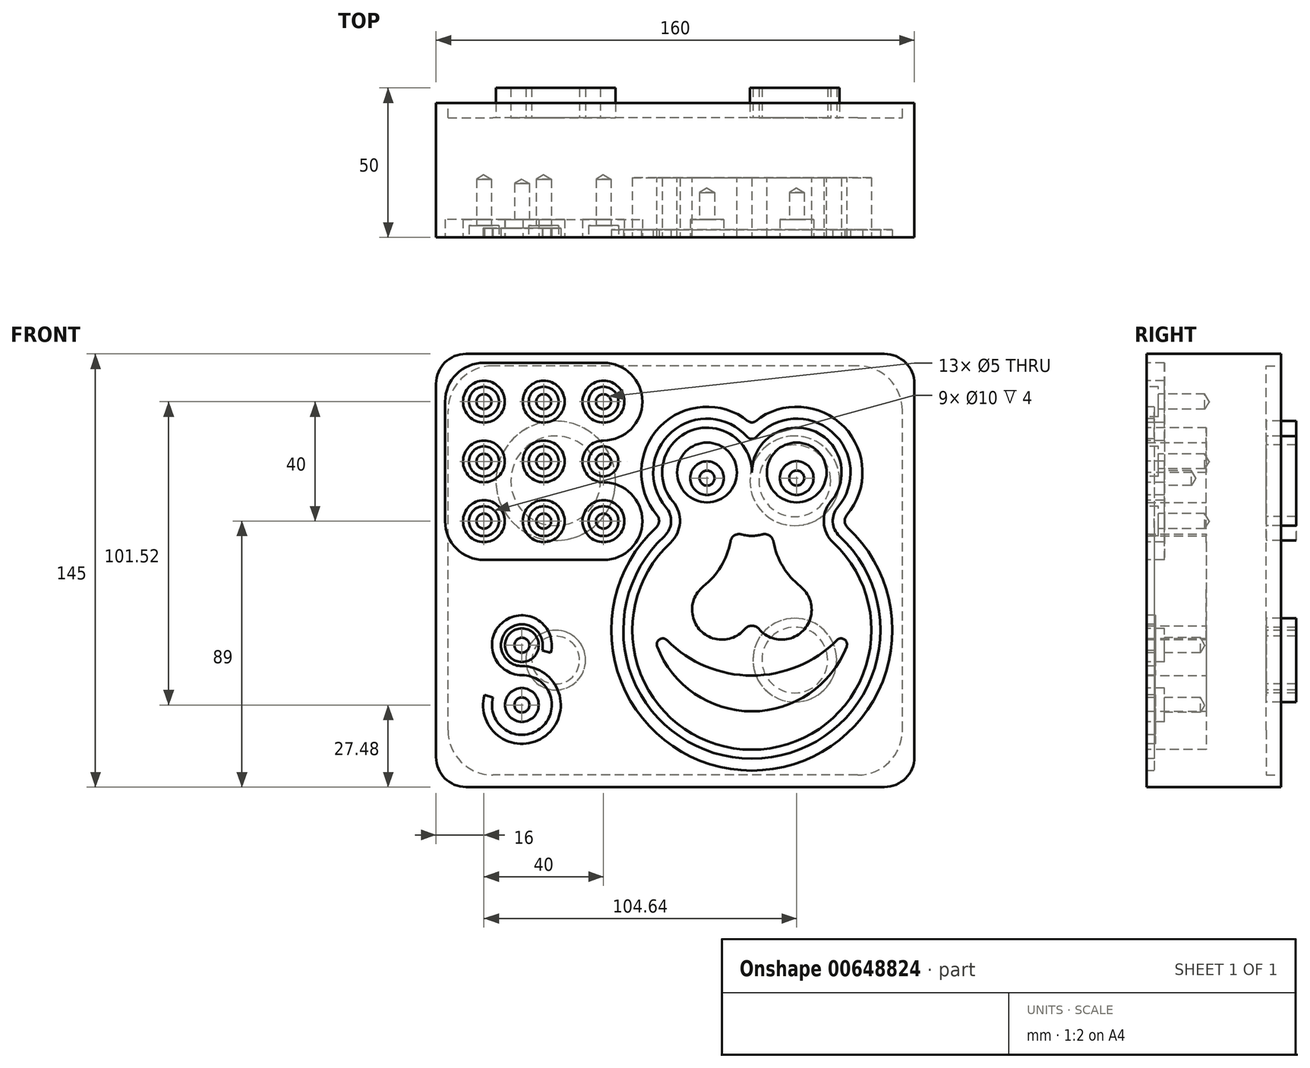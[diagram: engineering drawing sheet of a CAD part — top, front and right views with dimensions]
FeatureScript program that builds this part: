
annotation { "Feature Type Name" : "Feature", "Feature Type Description" : "" }
export const myFeature = defineFeature(function(context is Context, id is Id, definition is map)
    precondition{}
    {
        {
            var Q0;
            Q0=qCreatedBy(makeId("Front.planeOp"),FACE);
            var sketch = newSketch(context, id + "F0", { "sketchPlane" : qUnion([Q0])});
            skLineSegment(sketch, "E0.bottom", {"start": v(70, 72.5) * mm, "end": v(-70, 72.5) * mm});
            skLineSegment(sketch, "E0.top", {"start": v(70, -72.5) * mm, "end": v(-70, -72.5) * mm});
            skLineSegment(sketch, "E0.left", {"start": v(80, 62.5) * mm, "end": v(80, -62.5) * mm});
            skLineSegment(sketch, "E0.right", {"start": v(-80, 62.5) * mm, "end": v(-80, -62.5) * mm});
            skPoint(sketch, "E0.middle", {"position": v(0, 0) * mm});
            skPoint(sketch, "E1.visualSharp", {"position": v(-80, 72.5) * mm});
            skArc(sketch, "E1.filletArc", {"start": v(-70, 72.5) * mm, "mid": v(-77.07, 69.57) * mm, "end": v(-80, 62.5) * mm});
            skPoint(sketch, "E2.visualSharp", {"position": v(80, 72.5) * mm});
            skArc(sketch, "E2.filletArc", {"start": v(80, 62.5) * mm, "mid": v(77.07, 69.57) * mm, "end": v(70, 72.5) * mm});
            skPoint(sketch, "E3.visualSharp", {"position": v(80, -72.5) * mm});
            skArc(sketch, "E3.filletArc", {"start": v(70, -72.5) * mm, "mid": v(77.07, -69.57) * mm, "end": v(80, -62.5) * mm});
            skPoint(sketch, "E4.visualSharp", {"position": v(-80, -72.5) * mm});
            skArc(sketch, "E4.filletArc", {"start": v(-80, -62.5) * mm, "mid": v(-77.07, -69.57) * mm, "end": v(-70, -72.5) * mm});
            skSolve(sketch);
        }
        {
            var Q0;
            Q0 = qSketchRegion(id + "F0", true);
            extrude(context, id + "F1", {"entities" : qUnion([Q0]), "oppositeDirection" : true, "depth" : 45 * mm, "offsetDistance" : 25 * mm});
        }
        {
            var Q0;
            Q0=qCreatedBy(makeId("Front.planeOp"),FACE);
            cPlane(context, id + "F2", {"entities" : qUnion([Q0]), "cplaneType" : CPlaneType.OFFSET, "offset" : 40 * mm, "oppositeDirection" : true, "width" : 150 * mm, "height" : 150 * mm});
        }
        {
            var Q0;
            {var subQ0=sQuery(id+"F0.wireOp",EDGE,"E4.filletArc");var subQ1=sQuery(id+"F0.wireOp",EDGE,"E3.filletArc");var subQ2=sQuery(id+"F0.wireOp",EDGE,"E2.filletArc");var subQ3=sQuery(id+"F0.wireOp",EDGE,"E1.filletArc");var subQ4=sQuery(id+"F0.wireOp",EDGE,"E0.bottom");var subQ5=sQuery(id+"F0.wireOp",EDGE,"E0.right");var subQ6=sQuery(id+"F0.wireOp",EDGE,"E0.top");var subQ7=sQuery(id+"F0.wireOp",EDGE,"E0.left");Q0=makeQuery(id+"F6.boolean.opBoolean","SPLIT",FACE,{"disambiguationData":[TD([makeQuery(id+"F1.opExtrude","SWEPT_FACE",FACE,{"disambiguationData":[OSD([subQ4])]})])],"derivedFrom":makeQuery(id+"F1.opExtrude","CAP_FACE",FACE,{"disambiguationData":[OSD([subQ4,subQ6,subQ7,subQ5,subQ3,subQ2,subQ1,subQ0])],"isStart":false})});}
            var sketch = newSketch(context, id + "F3", { "sketchPlane" : qUnion([Q0])});
            skLineSegment(sketch, "E5.bottom", {"start": v(-61, -68.5) * mm, "end": v(61, -68.5) * mm});
            skLineSegment(sketch, "E5.top", {"start": v(-61, 68.5) * mm, "end": v(61, 68.5) * mm});
            skLineSegment(sketch, "E5.left", {"start": v(-76, -53.5) * mm, "end": v(-76, 53.5) * mm});
            skLineSegment(sketch, "E5.right", {"start": v(76, -53.5) * mm, "end": v(76, 53.5) * mm});
            skPoint(sketch, "E5.middle", {"position": v(0, 0) * mm});
            skPoint(sketch, "E6.visualSharp", {"position": v(-76, 68.5) * mm});
            skArc(sketch, "E6.filletArc", {"start": v(-61, 68.5) * mm, "mid": v(-71.6, 64.1) * mm, "end": v(-76, 53.5) * mm});
            skPoint(sketch, "E7.visualSharp", {"position": v(76, 68.5) * mm});
            skArc(sketch, "E7.filletArc", {"start": v(76, 53.5) * mm, "mid": v(71.6, 64.1) * mm, "end": v(61, 68.5) * mm});
            skPoint(sketch, "E8.visualSharp", {"position": v(76, -68.5) * mm});
            skArc(sketch, "E8.filletArc", {"start": v(61, -68.5) * mm, "mid": v(71.6, -64.1) * mm, "end": v(76, -53.5) * mm});
            skPoint(sketch, "E9.visualSharp", {"position": v(-76, -68.5) * mm});
            skArc(sketch, "E9.filletArc", {"start": v(-76, -53.5) * mm, "mid": v(-71.6, -64.1) * mm, "end": v(-61, -68.5) * mm});
            skSolve(sketch);
        }
        {
            var Q0;
            Q0 = qSketchRegion(id + "F3", true);
            extrude(context, id + "F4", {"entities" : qUnion([Q0]), "operationType" : NewBodyOperationType.REMOVE, "oppositeDirection" : true, "depth" : 5 * mm, "offsetDistance" : 25 * mm});
        }
        {
            var Q0;
            Q0=qCreatedBy(id+"F2.planeOp",FACE);
            var sketch = newSketch(context, id + "F5", { "sketchPlane" : qUnion([Q0])});
            skPoint(sketch, "E10.middle", {"position": v(0, 0) * mm});
            skCircle(sketch, "E11", {"center": v(-40, 30) * mm, "radius": 15 * mm});
            skCircle(sketch, "E12", {"center": v(-40, 30) * mm, "radius": 20 * mm});
            skCircle(sketch, "E13", {"center": v(40, 30) * mm, "radius": 12 * mm});
            skCircle(sketch, "E14", {"center": v(40, 30) * mm, "radius": 15 * mm});
            skCircle(sketch, "E15", {"center": v(-40, -30) * mm, "radius": 8 * mm});
            skCircle(sketch, "E16", {"center": v(-40, -30) * mm, "radius": 10 * mm});
            skCircle(sketch, "E17", {"center": v(40, -30) * mm, "radius": 11 * mm});
            skCircle(sketch, "E18", {"center": v(40, -30) * mm, "radius": 14 * mm});
            skSolve(sketch);
        }
        {
            var Q0;
            Q0 = qSketchRegion(id + "F5", true);
            extrude(context, id + "F6", {"entities" : qUnion([Q0]), "operationType" : NewBodyOperationType.ADD, "oppositeDirection" : true, "depth" : 10 * mm, "offsetDistance" : 25 * mm});
        }
        {
            var Q0;
            Q0=makeQuery(id+"F1.opExtrude","CAP_FACE",FACE,{"disambiguationData":[OSD([sQuery(id+"F0.wireOp",EDGE,"E0.bottom"),sQuery(id+"F0.wireOp",EDGE,"E0.top"),sQuery(id+"F0.wireOp",EDGE,"E0.left"),sQuery(id+"F0.wireOp",EDGE,"E0.right"),sQuery(id+"F0.wireOp",EDGE,"E1.filletArc"),sQuery(id+"F0.wireOp",EDGE,"E2.filletArc"),sQuery(id+"F0.wireOp",EDGE,"E3.filletArc"),sQuery(id+"F0.wireOp",EDGE,"E4.filletArc")])],"isStart":true});
            var sketch = newSketch(context, id + "F7", { "sketchPlane" : qUnion([Q0])});
            skPoint(sketch, "E19", {"position": v(-64, 56.5) * mm});
            skPoint(sketch, "E20.0.1.0", {"position": v(-64, 36.5) * mm});
            skPoint(sketch, "E20.0.2.0", {"position": v(-64, 16.5) * mm});
            skPoint(sketch, "E20.1.0.0", {"position": v(-44, 56.5) * mm});
            skPoint(sketch, "E20.1.1.0", {"position": v(-44, 36.5) * mm});
            skPoint(sketch, "E20.1.2.0", {"position": v(-44, 16.5) * mm});
            skPoint(sketch, "E20.2.0.0", {"position": v(-24, 56.5) * mm});
            skPoint(sketch, "E20.2.1.0", {"position": v(-24, 36.5) * mm});
            skPoint(sketch, "E20.2.2.0", {"position": v(-24, 16.5) * mm});
            skLineSegment(sketch, "E20.direction1", {"start": v(-64, 56.5) * mm, "end": v(-44, 56.5) * mm, "construction": true});
            skLineSegment(sketch, "E20.direction2", {"start": v(-64, 56.5) * mm, "end": v(-64, 36.5) * mm, "construction": true});
            skSolve(sketch);
        }
        {
            var Q0;
            Q0=makeQuery(id+"F7.imprint","IMPRINT",FACE,{"disambiguationData":[TD([[makeQuery(id+"F7.imprint","IMPRINT",EDGE,{"derivedFrom":makeQuery(id+"F1.opExtrude","CAP_EDGE",EDGE,{"disambiguationData":[OSD([sQuery(id+"F0.wireOp",EDGE,"E0.bottom")])],"isStart":true})}),1.0]])]});
            var sketch = newSketch(context, id + "F8", { "sketchPlane" : qUnion([Q0])});
            skLineSegment(sketch, "E21.bottom", {"start": v(-64, 69.5) * mm, "end": v(-24, 69.5) * mm});
            skLineSegment(sketch, "E21.top", {"start": v(-64, 3.5) * mm, "end": v(-24, 3.5) * mm});
            skLineSegment(sketch, "E21.left", {"start": v(-77, 56.5) * mm, "end": v(-77, 16.5) * mm});
            skPoint(sketch, "E21.middle", {"position": v(-44, 36.5) * mm});
            skPoint(sketch, "E22.visualSharp", {"position": v(-77, 69.5) * mm});
            skArc(sketch, "E22.filletArc", {"start": v(-64, 69.5) * mm, "mid": v(-73.2, 65.7) * mm, "end": v(-77, 56.5) * mm});
            skPoint(sketch, "E23.visualSharp", {"position": v(-77, 3.5) * mm});
            skArc(sketch, "E23.filletArc", {"start": v(-77, 16.5) * mm, "mid": v(-73.2, 7.3) * mm, "end": v(-64, 3.5) * mm});
            skPoint(sketch, "E24.visualSharp", {"position": v(-11, 3.5) * mm});
            skArc(sketch, "E24.filletArc", {"start": v(-24, 3.5) * mm, "mid": v(-11, 16.5) * mm, "end": v(-24, 29.5) * mm});
            skPoint(sketch, "E25.visualSharp", {"position": v(-11, 69.5) * mm});
            skArc(sketch, "E25.filletArc", {"start": v(-24, 43.5) * mm, "mid": v(-11, 56.5) * mm, "end": v(-24, 69.5) * mm});
            skArc(sketch, "E26", {"start": v(-24, 43.5) * mm, "mid": v(-31, 36.5) * mm, "end": v(-24, 29.5) * mm});
            skSolve(sketch);
        }
        {
            var Q0;
            Q0 = qSketchRegion(id + "F8", true);
            extrude(context, id + "F9", {"entities" : qUnion([Q0]), "operationType" : NewBodyOperationType.REMOVE, "oppositeDirection" : true, "depth" : 6 * mm, "offsetDistance" : 25 * mm});
        }
        {
            var Q0;
            Q0=makeQuery(id+"F7.imprint","IMPRINT",FACE,{"disambiguationData":[TD([[makeQuery(id+"F7.imprint","IMPRINT",EDGE,{"derivedFrom":makeQuery(id+"F1.opExtrude","CAP_EDGE",EDGE,{"disambiguationData":[OSD([sQuery(id+"F0.wireOp",EDGE,"E0.bottom")])],"isStart":true})}),1.0]])]});
            var sketch = newSketch(context, id + "F10", { "sketchPlane" : qUnion([Q0])});
            skCircle(sketch, "E27", {"center": v(-44, 56.5) * mm, "radius": 7 * mm});
            skCircle(sketch, "E28.0.1.0", {"center": v(-44, 36.5) * mm, "radius": 7 * mm});
            skCircle(sketch, "E28.0.2.0", {"center": v(-44, 16.5) * mm, "radius": 7 * mm});
            skCircle(sketch, "E28.1.0.0", {"center": v(-64, 56.5) * mm, "radius": 7 * mm});
            skCircle(sketch, "E28.1.1.0", {"center": v(-64, 36.5) * mm, "radius": 7 * mm});
            skCircle(sketch, "E28.1.2.0", {"center": v(-64, 16.5) * mm, "radius": 7 * mm});
            skCircle(sketch, "E29.1.0.0", {"center": v(-24, 56.5) * mm, "radius": 7 * mm});
            skCircle(sketch, "E30.0.1.0", {"center": v(-24, 16.5) * mm, "radius": 7 * mm});
            skLineSegment(sketch, "E30.direction2", {"start": v(-24, 56.5) * mm, "end": v(-24, 16.5) * mm, "construction": true});
            skSolve(sketch);
        }
        {
            var Q0;
            Q0 = qSketchRegion(id + "F10", true);
            extrude(context, id + "F11", {"entities" : qUnion([Q0]), "operationType" : NewBodyOperationType.ADD, "oppositeDirection" : true, "depth" : 6 * mm, "offsetDistance" : 25 * mm});
        }
        {
            var Q0;
            Q0=makeQuery(id+"F8.imprint","IMPRINT",FACE,{"disambiguationData":[TD([[makeQuery(id+"F8.imprint","IMPRINT",EDGE,{"derivedFrom":sQuery(id+"F8.wireOp",EDGE,"E21.bottom")}),-1.0]])]});
            var sketch = newSketch(context, id + "F12", { "sketchPlane" : qUnion([Q0])});
            skPoint(sketch, "E31", {"position": v(-64, 56.5) * mm});
            skPoint(sketch, "E32.0.1.0", {"position": v(-64, 36.5) * mm});
            skPoint(sketch, "E32.0.2.0", {"position": v(-64, 16.5) * mm});
            skPoint(sketch, "E32.1.0.0", {"position": v(-44, 56.5) * mm});
            skPoint(sketch, "E32.1.1.0", {"position": v(-44, 36.5) * mm});
            skPoint(sketch, "E32.1.2.0", {"position": v(-44, 16.5) * mm});
            skPoint(sketch, "E32.2.0.0", {"position": v(-24, 56.5) * mm});
            skPoint(sketch, "E32.2.1.0", {"position": v(-24, 36.5) * mm});
            skPoint(sketch, "E32.2.2.0", {"position": v(-24, 16.5) * mm});
            skLineSegment(sketch, "E32.direction1", {"start": v(-64, 56.5) * mm, "end": v(-44, 56.5) * mm, "construction": true});
            skLineSegment(sketch, "E32.direction2", {"start": v(-64, 56.5) * mm, "end": v(-64, 36.5) * mm, "construction": true});
            skSolve(sketch);
        }
        {
            var Q0;
            Q0=sQuery(id+"F12.wireOp",VERTEX,"E31");
            var Q1;
            Q1=sQuery(id+"F12.wireOp",VERTEX,"E32.1.0.0");
            var Q2;
            Q2=sQuery(id+"F12.wireOp",VERTEX,"E32.2.0.0");
            var Q3;
            Q3=sQuery(id+"F12.wireOp",VERTEX,"E32.0.1.0");
            var Q4;
            Q4=sQuery(id+"F8.wireOp",VERTEX,"E26.center");
            var Q5;
            Q5=sQuery(id+"F12.wireOp",VERTEX,"E32.1.2.0");
            var Q6;
            Q6=sQuery(id+"F12.wireOp",VERTEX,"E32.2.2.0");
            var Q7;
            Q7=sQuery(id+"F8.wireOp",VERTEX,"E21.middle");
            var Q8;
            Q8=sQuery(id+"F12.wireOp",VERTEX,"E32.0.2.0");
            var Q9;
            Q9=makeQuery(id+"F4.boolean.opBoolean","SPLIT",BODY,{"disambiguationData":[OD(0.0)],"derivedFrom":makeQuery(id+"F1.opExtrude","SWEPT_BODY",BODY,{"disambiguationData":[OSD([sQuery(id+"F0.wireOp",EDGE,"E0.bottom"),sQuery(id+"F0.wireOp",EDGE,"E0.top"),sQuery(id+"F0.wireOp",EDGE,"E0.left"),sQuery(id+"F0.wireOp",EDGE,"E0.right"),sQuery(id+"F0.wireOp",EDGE,"E1.filletArc"),sQuery(id+"F0.wireOp",EDGE,"E2.filletArc"),sQuery(id+"F0.wireOp",EDGE,"E3.filletArc"),sQuery(id+"F0.wireOp",EDGE,"E4.filletArc")])]})});
            hole(context, id + "F13", {"style" : HoleStyle.C_BORE, "endStyle" : HoleEndStyle.BLIND, "holeDiameter" : 5 * mm, "cBoreDiameter" : 10 * mm, "cBoreDepth" : 4 * mm, "majorDiameter" : 6 * mm, "holeDepth" : 19.48 * mm, "isTappedThrough" : true, "tappedDepth" : 12 * mm, "tapClearance" : 3, "locations" : qUnion([Q0, Q1, Q2, Q3, Q4, Q5, Q6, Q7, Q8]), "scope" : qUnion([Q9])});
        }
        {
            var Q0;
            Q0=makeQuery(id+"F8.imprint","IMPRINT",FACE,{"disambiguationData":[TD([[makeQuery(id+"F8.imprint","IMPRINT",EDGE,{"derivedFrom":sQuery(id+"F8.wireOp",EDGE,"E21.bottom")}),1.0]])]});
            var sketch = newSketch(context, id + "F14", { "sketchPlane" : qUnion([Q0])});
            skLineSegment(sketch, "E33", {"start": v(25.64, 51.55) * mm, "end": v(25.64, 32.8) * mm});
            skLineSegment(sketch, "E34", {"start": v(-2.76, -20) * mm, "end": v(55.32, -20) * mm});
            skLineSegment(sketch, "E35", {"start": v(40.64, 63.23) * mm, "end": v(40.64, 28.74) * mm});
            skLineSegment(sketch, "E36", {"start": v(10.64, 63.8) * mm, "end": v(10.64, 27.42) * mm});
            skLineSegment(sketch, "E37", {"start": v(10.64, 30.8) * mm, "end": v(40.64, 30.8) * mm});
            skLineSegment(sketch, "E38", {"start": v(10.64, 32.8) * mm, "end": v(40.64, 32.8) * mm});
            skArc(sketch, "E39", {"start": v(54.36, 21.15) * mm, "mid": v(52.42, 46.4) * mm, "end": v(27.14, 44.7) * mm});
            skArc(sketch, "E40", {"start": v(57.4, 18.56) * mm, "mid": v(56.42, 48.13) * mm, "end": v(26.89, 49.97) * mm});
            skArc(sketch, "E41.MirrorC", {"start": v(-3.08, 21.15) * mm, "mid": v(-1.14, 46.4) * mm, "end": v(24.14, 44.7) * mm});
            skArc(sketch, "E42.MirrorC", {"start": v(-6.13, 18.56) * mm, "mid": v(-5.14, 48.13) * mm, "end": v(24.39, 49.97) * mm});
            skLineSegment(sketch, "E43.trimOffspring", {"start": v(25.64, 27) * mm, "end": v(25.64, -20) * mm});
            skPoint(sketch, "E44.center.orphan", {"position": v(26.28, -20) * mm});
            skArc(sketch, "E45", {"start": v(-3.64, 11.49) * mm, "mid": v(25.64, -63) * mm, "end": v(54.92, 11.49) * mm});
            skArc(sketch, "E46", {"start": v(-6.37, 14.42) * mm, "mid": v(25.64, -67) * mm, "end": v(57.65, 14.42) * mm});
            skPoint(sketch, "E47.visualSharp", {"position": v(55.34, 16.43) * mm});
            skArc(sketch, "E47.filletArc", {"start": v(57.4, 18.56) * mm, "mid": v(56.7, 16.44) * mm, "end": v(57.65, 14.42) * mm});
            skPoint(sketch, "E48.visualSharp", {"position": v(-4.06, 16.43) * mm});
            skArc(sketch, "E48.filletArc", {"start": v(-6.37, 14.42) * mm, "mid": v(-5.42, 16.44) * mm, "end": v(-6.13, 18.56) * mm});
            skArc(sketch, "E49.filletArc", {"start": v(54.36, 21.15) * mm, "mid": v(52.7, 16.2) * mm, "end": v(54.92, 11.49) * mm});
            skArc(sketch, "E50.filletArc", {"start": v(-3.64, 11.49) * mm, "mid": v(-1.42, 16.2) * mm, "end": v(-3.08, 21.15) * mm});
            skPoint(sketch, "E51.visualSharp", {"position": v(25.64, 42.75) * mm});
            skArc(sketch, "E51.filletArc", {"start": v(24.14, 44.7) * mm, "mid": v(25.64, 44.03) * mm, "end": v(27.14, 44.7) * mm});
            skPoint(sketch, "E52.visualSharp", {"position": v(25.64, 48.9) * mm});
            skArc(sketch, "E52.filletArc", {"start": v(24.39, 49.97) * mm, "mid": v(25.64, 49.53) * mm, "end": v(26.89, 49.97) * mm});
            skArc(sketch, "E53", {"start": v(-1.6, 9.3) * mm, "mid": v(25.64, -60) * mm, "end": v(52.88, 9.3) * mm});
            skArc(sketch, "E54", {"start": v(25.64, 32.8) * mm, "mid": v(5.47, 46.88) * mm, "end": v(-0.8, 23.09) * mm});
            skArc(sketch, "E55", {"start": v(52.07, 23.09) * mm, "mid": v(45.81, 46.88) * mm, "end": v(25.64, 32.8) * mm});
            skPoint(sketch, "E56.visualSharp", {"position": v(38.06, 18.02) * mm});
            skArc(sketch, "E56.filletArc", {"start": v(52.07, 23.09) * mm, "mid": v(49.7, 16.03) * mm, "end": v(52.88, 9.3) * mm});
            skPoint(sketch, "E57.visualSharp", {"position": v(13.22, 18.02) * mm});
            skArc(sketch, "E57.filletArc", {"start": v(-1.6, 9.3) * mm, "mid": v(1.57, 16.03) * mm, "end": v(-0.8, 23.09) * mm});
            skSolve(sketch);
        }
        {
            var Q0;
            Q0 = qSketchRegion(id + "F14", true);
            extrude(context, id + "F15", {"entities" : qUnion([Q0]), "operationType" : NewBodyOperationType.REMOVE, "oppositeDirection" : true, "depth" : 2.6 * mm, "offsetDistance" : 25 * mm});
        }
        {
            var Q0;
            Q0=makeQuery(id+"F8.imprint","IMPRINT",FACE,{"disambiguationData":[TD([[makeQuery(id+"F8.imprint","IMPRINT",EDGE,{"derivedFrom":sQuery(id+"F8.wireOp",EDGE,"E21.bottom")}),1.0]])]});
            var sketch = newSketch(context, id + "F16", { "sketchPlane" : qUnion([Q0])});
            skLineSegment(sketch, "E58", {"start": v(25.64, 51.55) * mm, "end": v(25.64, 51.53) * mm});
            skLineSegment(sketch, "E59", {"start": v(-2.76, -20) * mm, "end": v(55.32, -20) * mm});
            skLineSegment(sketch, "E60", {"start": v(10.64, 30.8) * mm, "end": v(40.64, 30.8) * mm});
            skLineSegment(sketch, "E61.trimOffspring", {"start": v(25.64, 27) * mm, "end": v(25.64, -20) * mm});
            skPoint(sketch, "E62.center.orphan", {"position": v(26.28, -20) * mm});
            skPoint(sketch, "E63.visualSharp", {"position": v(55.34, 16.43) * mm});
            skPoint(sketch, "E64.visualSharp", {"position": v(-4.06, 16.43) * mm});
            skPoint(sketch, "E65.visualSharp", {"position": v(25.64, 42.75) * mm});
            skPoint(sketch, "E66.visualSharp", {"position": v(25.64, 48.9) * mm});
            skArc(sketch, "E67", {"start": v(25.64, 32.8) * mm, "mid": v(5.47, 46.88) * mm, "end": v(-0.8, 23.09) * mm});
            skArc(sketch, "E68", {"start": v(52.07, 23.09) * mm, "mid": v(45.81, 46.88) * mm, "end": v(25.64, 32.8) * mm});
            skPoint(sketch, "E69.visualSharp", {"position": v(38.06, 18.02) * mm});
            skArc(sketch, "E69.filletArc", {"start": v(52.07, 23.09) * mm, "mid": v(49.7, 16.03) * mm, "end": v(52.88, 9.3) * mm});
            skPoint(sketch, "E70.visualSharp", {"position": v(13.22, 18.02) * mm});
            skArc(sketch, "E70.filletArc", {"start": v(-1.6, 9.3) * mm, "mid": v(1.57, 16.03) * mm, "end": v(-0.8, 23.09) * mm});
            skLineSegment(sketch, "E71.trimOffspring", {"start": v(40.64, 32.8) * mm, "end": v(40.64, 28.74) * mm});
            skLineSegment(sketch, "E72.trimOffspring", {"start": v(25.64, 42.75) * mm, "end": v(25.64, 32.8) * mm});
            skArc(sketch, "E73", {"start": v(-1.6, 9.3) * mm, "mid": v(25.64, -60) * mm, "end": v(52.88, 9.3) * mm});
            skLineSegment(sketch, "E74.trimOffspring", {"start": v(10.64, 32.8) * mm, "end": v(10.64, 27.42) * mm});
            skSolve(sketch);
        }
        {
            var Q0;
            Q0 = qSketchRegion(id + "F16", true);
            extrude(context, id + "F17", {"entities" : qUnion([Q0]), "operationType" : NewBodyOperationType.REMOVE, "oppositeDirection" : true, "depth" : 20 * mm, "offsetDistance" : 25 * mm});
        }
        {
            var Q0;
            Q0=qCreatedBy(makeId("Front.planeOp"),FACE);
            cPlane(context, id + "F18", {"entities" : qUnion([Q0]), "cplaneType" : CPlaneType.OFFSET, "offset" : 20 * mm, "oppositeDirection" : true, "width" : 150 * mm, "height" : 150 * mm});
        }
        {
            var Q0;
            Q0=qCreatedBy(id+"F18.planeOp",FACE);
            var sketch = newSketch(context, id + "F19", { "sketchPlane" : qUnion([Q0])});
            skLineSegment(sketch, "E75", {"start": v(25.64, 51.55) * mm, "end": v(25.64, 30.8) * mm});
            skLineSegment(sketch, "E76", {"start": v(25.64, -21.16) * mm, "end": v(26.28, -21.16) * mm});
            skLineSegment(sketch, "E77", {"start": v(40.64, 63.23) * mm, "end": v(40.64, 28.74) * mm});
            skLineSegment(sketch, "E78", {"start": v(10.64, 63.8) * mm, "end": v(10.64, 27.42) * mm});
            skLineSegment(sketch, "E79.trimOffspring", {"start": v(25.64, 23.56) * mm, "end": v(25.64, 11.56) * mm});
            skPoint(sketch, "E80.center.orphan", {"position": v(26.28, -21.16) * mm});
            skPoint(sketch, "E81.visualSharp", {"position": v(55.34, 16.43) * mm});
            skPoint(sketch, "E82.visualSharp", {"position": v(-4.06, 16.43) * mm});
            skPoint(sketch, "E83.visualSharp", {"position": v(25.64, 42.75) * mm});
            skPoint(sketch, "E84.visualSharp", {"position": v(25.64, 48.9) * mm});
            skPoint(sketch, "E85.visualSharp", {"position": v(38.06, 18.02) * mm});
            skPoint(sketch, "E86.visualSharp", {"position": v(13.22, 18.02) * mm});
            skCircle(sketch, "E87", {"center": v(10.64, 32.8) * mm, "radius": 10 * mm});
            skCircle(sketch, "E88", {"center": v(40.64, 32.8) * mm, "radius": 10 * mm});
            skPoint(sketch, "E89.middle", {"position": v(25.64, -21.16) * mm});
            skArc(sketch, "E90", {"start": v(27.97, -19.58) * mm, "mid": v(42.8, -20.14) * mm, "end": v(41.86, -5.33) * mm});
            skArc(sketch, "E91", {"start": v(29.03, 12.05) * mm, "mid": v(25.64, 11.56) * mm, "end": v(22.25, 12.05) * mm});
            skPoint(sketch, "E92.start.orphan", {"position": v(34.84, 16.43) * mm});
            skPoint(sketch, "E93.end.orphan", {"position": v(59.84, 16.43) * mm});
            skArc(sketch, "E94", {"start": v(41.86, -5.33) * mm, "mid": v(35.98, 1.37) * mm, "end": v(32.83, 9.72) * mm});
            skArc(sketch, "E95.filletArc", {"start": v(32.83, 9.72) * mm, "mid": v(31.45, 11.73) * mm, "end": v(29.03, 12.05) * mm});
            skArc(sketch, "E96.MirrorCS", {"start": v(18.45, 9.72) * mm, "mid": v(19.83, 11.73) * mm, "end": v(22.25, 12.05) * mm});
            skArc(sketch, "E97.MirrorCS", {"start": v(9.42, -5.33) * mm, "mid": v(15.3, 1.37) * mm, "end": v(18.45, 9.72) * mm});
            skArc(sketch, "E98.MirrorCS", {"start": v(23.3, -19.58) * mm, "mid": v(8.48, -20.14) * mm, "end": v(9.42, -5.33) * mm});
            skArc(sketch, "E99", {"start": v(23.3, -19.58) * mm, "mid": v(25.64, -18.5) * mm, "end": v(27.97, -19.58) * mm});
            skPoint(sketch, "E100.orphan", {"position": v(35.64, -29.16) * mm});
            skPoint(sketch, "E101.orphan", {"position": v(15.64, -29.16) * mm});
            skLineSegment(sketch, "E102", {"start": v(15.64, -13.16) * mm, "end": v(35.64, -13.16) * mm});
            skLineSegment(sketch, "E103", {"start": v(25.64, 1.2) * mm, "end": v(25.64, 4.82) * mm});
            skPoint(sketch, "E104.orphan", {"position": v(25.64, 1.2) * mm});
            skArc(sketch, "E105", {"start": v(-2.77, -23.34) * mm, "mid": v(10.25, -32.1) * mm, "end": v(25.64, -35.18) * mm});
            skArc(sketch, "E106", {"start": v(25.64, -47.16) * mm, "mid": v(6.44, -41.22) * mm, "end": v(-6.05, -25.47) * mm});
            skArc(sketch, "E107.filletArc", {"start": v(-2.77, -23.34) * mm, "mid": v(-5.28, -23.07) * mm, "end": v(-6.05, -25.47) * mm});
            skArc(sketch, "E108.MirrorCS", {"start": v(25.64, -47.16) * mm, "mid": v(44.84, -41.22) * mm, "end": v(57.33, -25.47) * mm});
            skArc(sketch, "E109.MirrorCS", {"start": v(54.05, -23.34) * mm, "mid": v(41.03, -32.1) * mm, "end": v(25.64, -35.18) * mm});
            skArc(sketch, "E110.MirrorCS", {"start": v(54.05, -23.34) * mm, "mid": v(56.56, -23.07) * mm, "end": v(57.33, -25.47) * mm});
            skLineSegment(sketch, "E111.trimOffspring", {"start": v(25.5, 30.8) * mm, "end": v(25.64, 30.8) * mm});
            skPoint(sketch, "E112", {"position": v(10.64, 27.42) * mm});
            skPoint(sketch, "E113", {"position": v(40.64, 28.74) * mm});
            skLineSegment(sketch, "E114.trimOffspring", {"start": v(25.64, -47.16) * mm, "end": v(25.64, -49.86) * mm});
            skLineSegment(sketch, "E115.trimOffspring", {"start": v(25.64, -13.16) * mm, "end": v(25.64, -21.16) * mm});
            skLineSegment(sketch, "E116.trimOffspring", {"start": v(25.64, 4.82) * mm, "end": v(25.64, 1.2) * mm});
            skPoint(sketch, "E117.orphan", {"position": v(-2.76, -21.16) * mm});
            skPoint(sketch, "E118.orphan", {"position": v(55.32, -21.16) * mm});
            skSolve(sketch);
        }
        {
            var Q0;
            Q0 = qSketchRegion(id + "F19", true);
            extrude(context, id + "F20", {"entities" : qUnion([Q0]), "depth" : 20 * mm, "hasOffset" : true, "offsetDistance" : 20 * mm});
        }
        {
            var Q0;
            Q0=qCreatedBy(makeId("Front.planeOp"),FACE);
            var sketch = newSketch(context, id + "F21", { "sketchPlane" : qUnion([Q0])});
            skLineSegment(sketch, "E119", {"start": v(25.64, 51.55) * mm, "end": v(25.64, 30.8) * mm});
            skLineSegment(sketch, "E120", {"start": v(25.64, -21.16) * mm, "end": v(26.28, -21.16) * mm});
            skLineSegment(sketch, "E121", {"start": v(40.64, 63.23) * mm, "end": v(40.64, 28.75) * mm});
            skLineSegment(sketch, "E122", {"start": v(10.64, 63.8) * mm, "end": v(10.64, 27.42) * mm});
            skLineSegment(sketch, "E123.trimOffspring", {"start": v(25.64, 23.56) * mm, "end": v(25.64, 11.56) * mm});
            skPoint(sketch, "E124.center.orphan", {"position": v(26.28, -21.16) * mm});
            skPoint(sketch, "E125.visualSharp", {"position": v(28.61, 18.88) * mm});
            skPoint(sketch, "E126.visualSharp", {"position": v(-30.78, 18.88) * mm});
            skPoint(sketch, "E127.visualSharp", {"position": v(25.64, 42.75) * mm});
            skPoint(sketch, "E128.visualSharp", {"position": v(-1.08, 51.35) * mm});
            skArc(sketch, "E129", {"start": v(25.5, 30.8) * mm, "mid": v(25.6, 31.8) * mm, "end": v(25.64, 32.8) * mm});
            skPoint(sketch, "E130.visualSharp", {"position": v(11.33, 20.48) * mm});
            skPoint(sketch, "E131.visualSharp", {"position": v(13.22, 18.03) * mm});
            skCircle(sketch, "E132", {"center": v(10.64, 32.8) * mm, "radius": 10 * mm});
            skCircle(sketch, "E133", {"center": v(40.64, 32.8) * mm, "radius": 10 * mm});
            skPoint(sketch, "E134.middle", {"position": v(25.64, -21.16) * mm});
            skArc(sketch, "E135", {"start": v(27.97, -19.58) * mm, "mid": v(42.8, -20.14) * mm, "end": v(41.86, -5.33) * mm});
            skArc(sketch, "E136", {"start": v(29.03, 12.05) * mm, "mid": v(25.64, 11.56) * mm, "end": v(22.25, 12.05) * mm});
            skPoint(sketch, "E137.start.orphan", {"position": v(8.11, 18.88) * mm});
            skPoint(sketch, "E138.end.orphan", {"position": v(33.11, 18.88) * mm});
            skArc(sketch, "E139", {"start": v(41.86, -5.33) * mm, "mid": v(35.98, 1.38) * mm, "end": v(32.83, 9.72) * mm});
            skArc(sketch, "E140.filletArc", {"start": v(32.83, 9.72) * mm, "mid": v(31.45, 11.73) * mm, "end": v(29.03, 12.05) * mm});
            skArc(sketch, "E141.MirrorCS", {"start": v(18.45, 9.72) * mm, "mid": v(19.83, 11.73) * mm, "end": v(22.25, 12.05) * mm});
            skArc(sketch, "E142.MirrorCS", {"start": v(9.42, -5.33) * mm, "mid": v(15.3, 1.38) * mm, "end": v(18.45, 9.72) * mm});
            skArc(sketch, "E143.MirrorCS", {"start": v(23.3, -19.58) * mm, "mid": v(8.48, -20.14) * mm, "end": v(9.42, -5.33) * mm});
            skArc(sketch, "E144", {"start": v(23.3, -19.58) * mm, "mid": v(25.64, -18.49) * mm, "end": v(27.97, -19.58) * mm});
            skLineSegment(sketch, "E145", {"start": v(15.64, -13.16) * mm, "end": v(35.64, -13.16) * mm});
            skLineSegment(sketch, "E146", {"start": v(25.64, 1.2) * mm, "end": v(25.64, 4.82) * mm});
            skPoint(sketch, "E147.orphan", {"position": v(25.64, 1.2) * mm});
            skArc(sketch, "E148", {"start": v(-2.77, -23.34) * mm, "mid": v(10.25, -32.1) * mm, "end": v(25.64, -35.18) * mm});
            skArc(sketch, "E149", {"start": v(25.64, -47.16) * mm, "mid": v(6.44, -41.22) * mm, "end": v(-6.05, -25.47) * mm});
            skArc(sketch, "E150.filletArc", {"start": v(-2.77, -23.34) * mm, "mid": v(-5.28, -23.07) * mm, "end": v(-6.05, -25.47) * mm});
            skArc(sketch, "E151.MirrorCS", {"start": v(54.05, -23.34) * mm, "mid": v(41.03, -32.1) * mm, "end": v(25.64, -35.18) * mm});
            skArc(sketch, "E152.MirrorCS", {"start": v(27.32, -20.89) * mm, "mid": v(29.83, -20.62) * mm, "end": v(30.6, -23.02) * mm});
            skLineSegment(sketch, "E153.trimOffspring", {"start": v(25.5, 30.8) * mm, "end": v(25.64, 30.8) * mm});
            skPoint(sketch, "E154", {"position": v(10.64, 27.42) * mm});
            skPoint(sketch, "E155", {"position": v(40.64, 28.75) * mm});
            skLineSegment(sketch, "E156.trimOffspring", {"start": v(-1.08, -47.16) * mm, "end": v(-1.08, -49.85) * mm});
            skLineSegment(sketch, "E157.trimOffspring", {"start": v(25.64, -13.16) * mm, "end": v(25.64, -21.16) * mm});
            skLineSegment(sketch, "E158.trimOffspring", {"start": v(25.64, 4.82) * mm, "end": v(25.64, 1.2) * mm});
            skPoint(sketch, "E159", {"position": v(10.64, 30.9) * mm});
            skPoint(sketch, "E160", {"position": v(40.64, 30.93) * mm});
            skSolve(sketch);
        }
        {
            var Q0;
            Q0=sQuery(id+"F21.wireOp",VERTEX,"E159");
            var Q1;
            Q1=sQuery(id+"F21.wireOp",VERTEX,"E160");
            var Q2;
            Q2=makeQuery(id+"F20.opExtrude","SWEPT_BODY",BODY,{"disambiguationData":[OSD([sQuery(id+"F19.wireOp",EDGE,"E87")])]});
            var Q3;
            Q3=makeQuery(id+"F20.opExtrude","SWEPT_BODY",BODY,{"disambiguationData":[OSD([sQuery(id+"F19.wireOp",EDGE,"E88")])]});
            hole(context, id + "F22", {"style" : HoleStyle.C_BORE, "endStyle" : HoleEndStyle.BLIND, "standardTappedOrClearance" : lookupTablePath({ "fit" : "Normal", "standard" : "ISO", "engagement" : "75%", "pitch" : "1 mm", "size" : "M6", "type" : "Tapped" }), "standardBlindInLast" : lookupTablePath({ "fit" : "Standard", "standard" : "ISO", "engagement" : "75%", "pitch" : "1 mm", "size" : "M6", "type" : "Tapped" }), "holeDiameter" : 5 * mm, "cBoreDiameter" : 11.25 * mm, "cBoreDepth" : 6 * mm, "majorDiameter" : 6 * mm, "showTappedDepth" : true, "holeDepth" : 15 * mm, "isTappedThrough" : true, "tappedDepth" : 12 * mm, "tapClearance" : 3, "startFromSketch" : true, "locations" : qUnion([Q0, Q1]), "scope" : qUnion([Q2, Q3])});
        }
        {
            var Q0;
            Q0=qCreatedBy(makeId("Front.planeOp"),FACE);
            var sketch = newSketch(context, id + "F23", { "sketchPlane" : qUnion([Q0])});
            skPoint(sketch, "E161", {"position": v(3.06, -33.28) * mm});
            skPoint(sketch, "E162", {"position": v(13.61, -39.4) * mm});
            skPoint(sketch, "E163.MirrorP", {"position": v(37.67, -39.4) * mm});
            skPoint(sketch, "E164.MirrorP", {"position": v(48.22, -33.28) * mm});
            skSolve(sketch);
        }
        {
            var Q0;
            Q0=makeQuery(id+"F0.imprint","IMPRINT",FACE,{"disambiguationData":[TD([[makeQuery(id+"F0.imprint","IMPRINT",EDGE,{"derivedFrom":sQuery(id+"F0.wireOp",EDGE,"E0.bottom")}),1.0]])]});
            var sketch = newSketch(context, id + "F24", { "sketchPlane" : qUnion([Q0])});
            skPoint(sketch, "E165", {"position": v(2.94, -33.2) * mm});
            skPoint(sketch, "E166", {"position": v(13.49, -39.32) * mm});
            skPoint(sketch, "E167.MirrorP", {"position": v(37.55, -39.32) * mm});
            skPoint(sketch, "E168.MirrorP", {"position": v(48.1, -33.2) * mm});
            skSolve(sketch);
        }
        {
            var Q0;
            Q0=makeQuery(id+"F7.imprint","IMPRINT",FACE,{"disambiguationData":[TD([[makeQuery(id+"F7.imprint","IMPRINT",EDGE,{"derivedFrom":makeQuery(id+"F1.opExtrude","CAP_EDGE",EDGE,{"disambiguationData":[OSD([sQuery(id+"F0.wireOp",EDGE,"E0.bottom")])],"isStart":true})}),1.0]])]});
            var sketch = newSketch(context, id + "F25", { "sketchPlane" : qUnion([Q0])});
            skLineSegment(sketch, "E169", {"start": v(-51.3, -25.02) * mm, "end": v(-58.3, -25.02) * mm});
            skLineSegment(sketch, "E170", {"start": v(-51.3, -59.61) * mm, "end": v(-51.3, -58.02) * mm});
            skArc(sketch, "E171", {"start": v(-41.64, -27.6) * mm, "mid": v(-57.39, -17.09) * mm, "end": v(-51.3, -35.02) * mm});
            skArc(sketch, "E172", {"start": v(-44.54, -26.83) * mm, "mid": v(-55.56, -19.47) * mm, "end": v(-51.3, -32.02) * mm});
            skLineSegment(sketch, "E173", {"start": v(-44.54, -26.83) * mm, "end": v(-41.64, -27.6) * mm});
            skArc(sketch, "E174", {"start": v(-51.3, -32.02) * mm, "mid": v(-43.39, -55.33) * mm, "end": v(-63.86, -41.66) * mm});
            skArc(sketch, "E175", {"start": v(-51.3, -35.02) * mm, "mid": v(-45.2, -52.94) * mm, "end": v(-60.97, -42.48) * mm});
            skLineSegment(sketch, "E176", {"start": v(-60.97, -42.48) * mm, "end": v(-63.86, -41.66) * mm});
            skSolve(sketch);
        }
        {
            var Q0;
            Q0 = qSketchRegion(id + "F25", true);
            extrude(context, id + "F26", {"entities" : qUnion([Q0]), "operationType" : NewBodyOperationType.REMOVE, "oppositeDirection" : true, "depth" : 3 * mm, "offsetDistance" : 25 * mm});
        }
        {
            var Q0;
            Q0=makeQuery(id+"F7.imprint","IMPRINT",FACE,{"disambiguationData":[TD([[makeQuery(id+"F7.imprint","IMPRINT",EDGE,{"derivedFrom":makeQuery(id+"F1.opExtrude","CAP_EDGE",EDGE,{"disambiguationData":[OSD([sQuery(id+"F0.wireOp",EDGE,"E0.bottom")])],"isStart":true})}),1.0]])]});
            var sketch = newSketch(context, id + "F27", { "sketchPlane" : qUnion([Q0])});
            skLineSegment(sketch, "E177", {"start": v(-51.3, -25.02) * mm, "end": v(-58.3, -25.02) * mm});
            skLineSegment(sketch, "E178", {"start": v(-51.3, -58.02) * mm, "end": v(-51.3, -22.82) * mm});
            skArc(sketch, "E179", {"start": v(-41.64, -27.6) * mm, "mid": v(-57.39, -17.09) * mm, "end": v(-51.3, -35.02) * mm});
            skArc(sketch, "E180", {"start": v(-44.54, -26.83) * mm, "mid": v(-55.56, -19.47) * mm, "end": v(-51.3, -32.02) * mm});
            skLineSegment(sketch, "E181", {"start": v(-44.54, -26.83) * mm, "end": v(-41.64, -27.6) * mm});
            skArc(sketch, "E182", {"start": v(-51.3, -32.02) * mm, "mid": v(-43.39, -55.33) * mm, "end": v(-63.86, -41.66) * mm});
            skArc(sketch, "E183", {"start": v(-51.3, -35.02) * mm, "mid": v(-45.2, -52.94) * mm, "end": v(-60.97, -42.48) * mm});
            skLineSegment(sketch, "E184", {"start": v(-60.97, -42.48) * mm, "end": v(-63.86, -41.66) * mm});
            skSolve(sketch);
        }
        {
            var Q0;
            Q0=sQuery(id+"F27.wireOp",VERTEX,"E179.center");
            var Q1;
            Q1=sQuery(id+"F27.wireOp",VERTEX,"E183.center");
            var Q2;
            Q2=makeQuery(id+"F4.boolean.opBoolean","SPLIT",BODY,{"disambiguationData":[OD(0.0)],"derivedFrom":makeQuery(id+"F1.opExtrude","SWEPT_BODY",BODY,{"disambiguationData":[OSD([sQuery(id+"F0.wireOp",EDGE,"E0.bottom"),sQuery(id+"F0.wireOp",EDGE,"E0.top"),sQuery(id+"F0.wireOp",EDGE,"E0.left"),sQuery(id+"F0.wireOp",EDGE,"E0.right"),sQuery(id+"F0.wireOp",EDGE,"E1.filletArc"),sQuery(id+"F0.wireOp",EDGE,"E2.filletArc"),sQuery(id+"F0.wireOp",EDGE,"E3.filletArc"),sQuery(id+"F0.wireOp",EDGE,"E4.filletArc")])]})});
            hole(context, id + "F28", {"style" : HoleStyle.C_BORE, "endStyle" : HoleEndStyle.BLIND, "standardTappedOrClearance" : lookupTablePath({ "fit" : "Normal", "standard" : "ISO", "engagement" : "75%", "pitch" : "1 mm", "size" : "M6", "type" : "Tapped" }), "standardBlindInLast" : lookupTablePath({ "fit" : "Standard", "standard" : "ISO", "engagement" : "75%", "pitch" : "1 mm", "size" : "M6", "type" : "Tapped" }), "holeDiameter" : 5 * mm, "cBoreDiameter" : 11.25 * mm, "cBoreDepth" : 6 * mm, "majorDiameter" : 6 * mm, "showTappedDepth" : true, "holeDepth" : 18 * mm, "isTappedThrough" : true, "tappedDepth" : 15 * mm, "tapClearance" : 3, "locations" : qUnion([Q0, Q1]), "scope" : qUnion([Q2])});
        }
        {
            var Q0;
            Q0=qCreatedBy(makeId("Front.planeOp"),FACE);
            var sketch = newSketch(context, id + "F29", { "sketchPlane" : qUnion([Q0])});
            skPoint(sketch, "E185", {"position": v(35.71, -13.16) * mm});
            skPoint(sketch, "E186", {"position": v(15.64, -13.16) * mm});
            skSolve(sketch);
        }
        {
            var Q0;
            Q0=sQuery(id+"F29.wireOp",VERTEX,"E185");
            var Q1;
            Q1=sQuery(id+"F29.wireOp",VERTEX,"E186");
            var Q2;
            Q2=makeQuery(id+"F1.opExtrude","SWEPT_BODY",BODY,{"disambiguationData":[OSD([sQuery(id+"F0.wireOp",EDGE,"E0.bottom"),sQuery(id+"F0.wireOp",EDGE,"E0.top"),sQuery(id+"F0.wireOp",EDGE,"E0.left"),sQuery(id+"F0.wireOp",EDGE,"E0.right"),sQuery(id+"F0.wireOp",EDGE,"E1.filletArc"),sQuery(id+"F0.wireOp",EDGE,"E2.filletArc"),sQuery(id+"F0.wireOp",EDGE,"E3.filletArc"),sQuery(id+"F0.wireOp",EDGE,"E4.filletArc")])]});
            hole(context, id + "F30", {"style" : HoleStyle.C_BORE, "endStyle" : HoleEndStyle.BLIND, "standardTappedOrClearance" : lookupTablePath({ "standard" : "ISO", "engagement" : "75%", "pitch" : "1 mm", "size" : "M6", "type" : "Tapped" }), "standardBlindInLast" : lookupTablePath({ "standard" : "ISO", "engagement" : "75%", "pitch" : "1 mm", "size" : "M6", "type" : "Tapped" }), "holeDiameter" : 5 * mm, "cBoreDiameter" : 11.25 * mm, "cBoreDepth" : 6 * mm, "majorDiameter" : 6 * mm, "showTappedDepth" : true, "holeDepth" : 15 * mm, "isTappedThrough" : true, "tappedDepth" : 12 * mm, "tapClearance" : 3, "startFromSketch" : true, "locations" : qUnion([Q0, Q1]), "scope" : qUnion([Q2])});
        }
        {
            var Q0;
            Q0=sQuery(id+"F24.wireOp",VERTEX,"E165");
            var Q1;
            Q1=sQuery(id+"F23.wireOp",VERTEX,"E162");
            var Q2;
            Q2=sQuery(id+"F23.wireOp",VERTEX,"E163.MirrorP");
            var Q3;
            Q3=sQuery(id+"F23.wireOp",VERTEX,"E164.MirrorP");
            var Q4;
            Q4=makeQuery(id+"F1.opExtrude","SWEPT_BODY",BODY,{"disambiguationData":[OSD([sQuery(id+"F0.wireOp",EDGE,"E0.bottom"),sQuery(id+"F0.wireOp",EDGE,"E0.top"),sQuery(id+"F0.wireOp",EDGE,"E0.left"),sQuery(id+"F0.wireOp",EDGE,"E0.right"),sQuery(id+"F0.wireOp",EDGE,"E1.filletArc"),sQuery(id+"F0.wireOp",EDGE,"E2.filletArc"),sQuery(id+"F0.wireOp",EDGE,"E3.filletArc"),sQuery(id+"F0.wireOp",EDGE,"E4.filletArc")])]});
            hole(context, id + "F31", {"style" : HoleStyle.SIMPLE, "endStyle" : HoleEndStyle.BLIND, "standardTappedOrClearance" : lookupTablePath({ "standard" : "ISO", "engagement" : "75%", "pitch" : "1 mm", "size" : "M6", "type" : "Tapped" }), "standardBlindInLast" : lookupTablePath({ "standard" : "ISO", "engagement" : "75%", "pitch" : "1 mm", "size" : "M6", "type" : "Tapped" }), "holeDiameter" : 5 * mm, "majorDiameter" : 6 * mm, "showTappedDepth" : true, "holeDepth" : 15 * mm, "isTappedThrough" : true, "tappedDepth" : 12 * mm, "tapClearance" : 3, "startFromSketch" : true, "locations" : qUnion([Q0, Q1, Q2, Q3]), "scope" : qUnion([Q4])});
        }
    });
